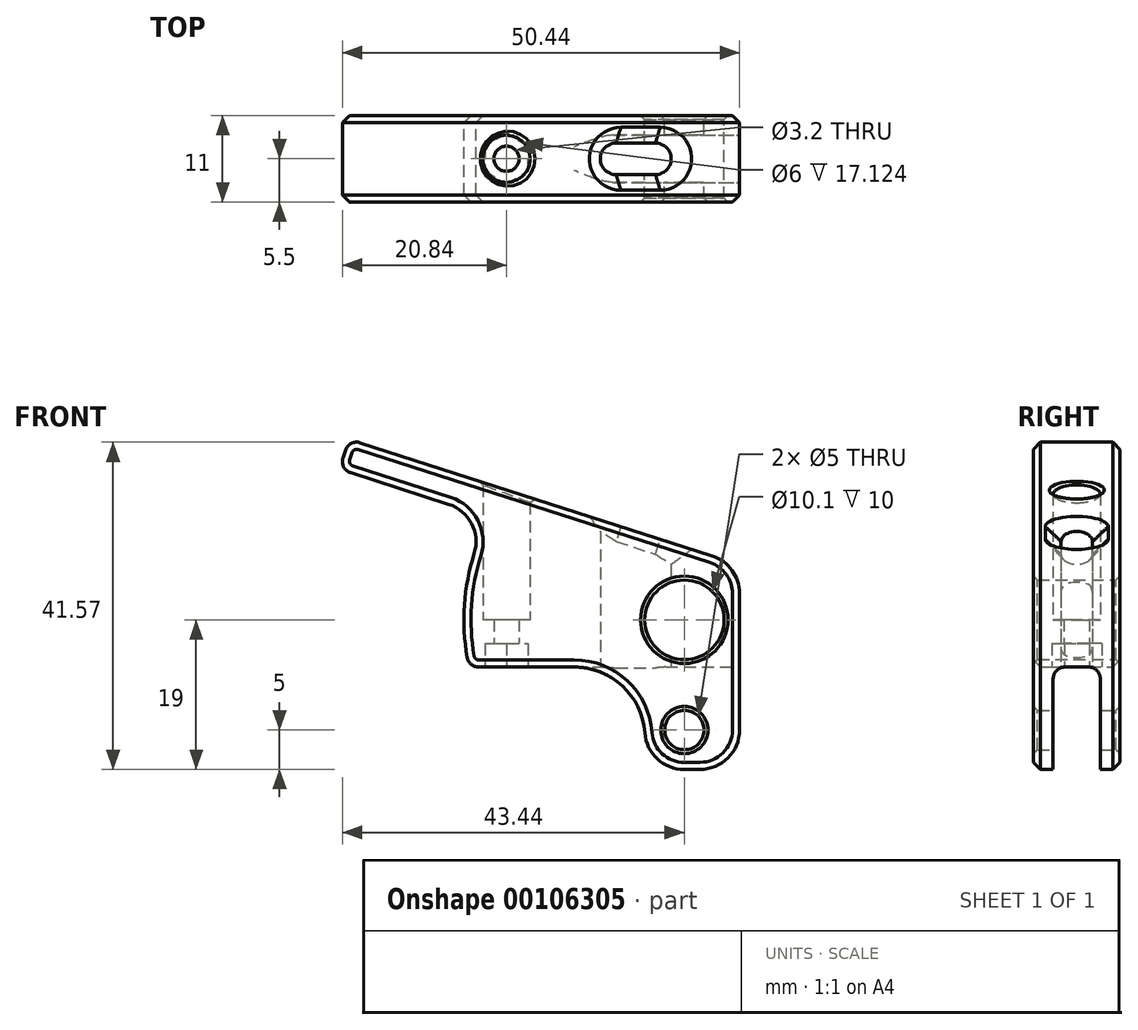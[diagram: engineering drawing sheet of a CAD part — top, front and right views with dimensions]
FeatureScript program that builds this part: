
annotation { "Feature Type Name" : "Feature", "Feature Type Description" : "" }
export const myFeature = defineFeature(function(context is Context, id is Id, definition is map)
    precondition{}
    {
        {
            var Q0;
            Q0=qCreatedBy(makeId("Front.planeOp"),FACE);
            var sketch = newSketch(context, id + "F0", { "sketchPlane" : qUnion([Q0])});
            skCircle(sketch, "E0", {"center": v(0, 0) * mm, "radius": 5.05 * mm});
            skCircle(sketch, "E1", {"center": v(0, -14) * mm, "radius": 2.5 * mm});
            skLineSegment(sketch, "E2.left", {"start": v(7, 7) * mm, "end": v(7, -19) * mm});
            skLineSegment(sketch, "E3.bottom", {"start": v(7, -19) * mm, "end": v(-5, -19) * mm});
            skLineSegment(sketch, "E3.right", {"start": v(-5, -19) * mm, "end": v(-5, -6) * mm});
            skLineSegment(sketch, "E4.trimOffspring", {"start": v(-5, -6) * mm, "end": v(-27.35, -6) * mm});
            skArc(sketch, "E5", {"start": v(-24.79, 13.02) * mm, "mid": v(-27.75, 3.74) * mm, "end": v(-27.35, -6) * mm});
            skLineSegment(sketch, "E6", {"start": v(-24.79, 13.02) * mm, "end": v(-43.83, 19.15) * mm});
            skLineSegment(sketch, "E7", {"start": v(-43.83, 19.15) * mm, "end": v(-42.6, 22.96) * mm});
            skLineSegment(sketch, "E8", {"start": v(-42.6, 22.96) * mm, "end": v(7, 7) * mm});
            skSolve(sketch);
        }
        {
            var Q0;
            Q0=qSketchRegion(id+"F0",true);
            extrude(context, id + "F1", {"entities" : qUnion([Q0]), "endBound" : BoundingType.SYMMETRIC, "depth" : 11 * mm});
        }
        {
            var Q0;
            Q0=makeQuery(id+"F1.opExtrude","SWEPT_FACE",FACE,{"disambiguationData":[OSD([sQuery(id+"F0.wireOp",EDGE,"E3.bottom")])]});
            var sketch = newSketch(context, id + "F2", { "sketchPlane" : qUnion([Q0])});
            skLineSegment(sketch, "E9.bottom", {"start": v(7, 3) * mm, "end": v(-7, 3) * mm});
            skLineSegment(sketch, "E9.top", {"start": v(7, -3) * mm, "end": v(-7, -3) * mm});
            skLineSegment(sketch, "E9.left", {"start": v(7, 3) * mm, "end": v(7, -3) * mm});
            skLineSegment(sketch, "E9.right", {"start": v(-7, 3) * mm, "end": v(-7, -3) * mm});
            skPoint(sketch, "E9.middle", {"position": v(0, 0) * mm});
            skSolve(sketch);
        }
        {
            var Q0;
            Q0=qSketchRegion(id+"F2",true);
            var Q1;
            Q1=makeQuery(id+"F1.opExtrude","SWEPT_FACE",FACE,{"disambiguationData":[OSD([sQuery(id+"F0.wireOp",EDGE,"E4.trimOffspring")])]});
            extrude(context, id + "F3", {"entities" : qUnion([Q0]), "operationType" : NewBodyOperationType.REMOVE, "endBound" : BoundingType.UP_TO_SURFACE, "oppositeDirection" : true, "endBoundEntityFace" : qUnion([Q1]), "depth" : 25 * mm});
        }
        {
            var Q0;
            Q0=makeQuery(id+"F3.boolean.opBoolean","MERGE",FACE,{"derivedFrom":[makeQuery(id+"F1.opExtrude","SWEPT_FACE",FACE,{"disambiguationData":[OSD([sQuery(id+"F0.wireOp",EDGE,"E4.trimOffspring")])]}),makeQuery(id+"F3.opExtrude","CAP_FACE",FACE,{"disambiguationData":[OSD([sQuery(id+"F2.wireOp",EDGE,"E9.bottom"),sQuery(id+"F2.wireOp",EDGE,"E9.top"),sQuery(id+"F2.wireOp",EDGE,"E9.left"),sQuery(id+"F2.wireOp",EDGE,"E9.right")])],"isStart":false})]});
            var sketch = newSketch(context, id + "F4", { "sketchPlane" : qUnion([Q0])});
            skLineSegment(sketch, "E10.bottom", {"start": v(-3.68, -2) * mm, "end": v(-8.68, -2) * mm});
            skLineSegment(sketch, "E10.top", {"start": v(-3.68, 2) * mm, "end": v(-8.68, 2) * mm});
            skPoint(sketch, "E10.middle", {"position": v(-6.18, 0) * mm});
            skArc(sketch, "E11", {"start": v(-8.68, 2) * mm, "mid": v(-10.68, 0) * mm, "end": v(-8.68, -2) * mm});
            skArc(sketch, "E12", {"start": v(-3.68, -2) * mm, "mid": v(-1.68, 0) * mm, "end": v(-3.68, 2) * mm});
            skSolve(sketch);
        }
        {
            var Q0;
            Q0=qSketchRegion(id+"F4",true);
            extrude(context, id + "F5", {"entities" : qUnion([Q0]), "operationType" : NewBodyOperationType.REMOVE, "endBound" : BoundingType.THROUGH_ALL, "oppositeDirection" : true, "depth" : 25 * mm});
        }
        {
            var Q0;
            {var subQ0=sQuery(id+"F0.wireOp",EDGE,"E4.trimOffspring");var subQ2=sQuery(id+"F2.wireOp",EDGE,"E9.bottom");var subQ3=sQuery(id+"F0.wireOp",EDGE,"E3.right");Q0=makeQuery(id+"F3.boolean.opBoolean","SPLIT",EDGE,{"disambiguationData":[TD([makeQuery(id+"F3.opExtrude","SWEPT_FACE",FACE,{"disambiguationData":[OSD([subQ2])]})])],"derivedFrom":makeQuery(id+"F1.opExtrude","SWEPT_EDGE",EDGE,{"disambiguationData":[OSD([subQ3,subQ0])]})});}
            var Q1;
            {var subQ0=sQuery(id+"F0.wireOp",EDGE,"E4.trimOffspring");var subQ1=sQuery(id+"F0.wireOp",EDGE,"E3.right");var subQ3=sQuery(id+"F2.wireOp",EDGE,"E9.top");Q1=makeQuery(id+"F3.boolean.opBoolean","SPLIT",EDGE,{"disambiguationData":[TD([makeQuery(id+"F3.opExtrude","SWEPT_FACE",FACE,{"disambiguationData":[OSD([subQ3])]})])],"derivedFrom":makeQuery(id+"F1.opExtrude","SWEPT_EDGE",EDGE,{"disambiguationData":[OSD([subQ1,subQ0])]})});}
            fillet(context, id + "F6", {"entities" : qUnion([Q0, Q1]), "radius" : 9 * mm, "tangentPropagation" : true, "allowEdgeOverflow" : false});
        }
        {
            var Q0;
            {var subQ0=sQuery(id+"F0.wireOp",EDGE,"E3.right");var subQ1=sQuery(id+"F0.wireOp",EDGE,"E3.bottom");Q0=makeQuery(id+"F3.boolean.opBoolean","SPLIT",EDGE,{"disambiguationData":[TD([makeQuery(id+"F3.opExtrude","SWEPT_FACE",FACE,{"disambiguationData":[OSD([sQuery(id+"F2.wireOp",EDGE,"E9.bottom")])]})])],"derivedFrom":makeQuery(id+"F1.opExtrude","SWEPT_EDGE",EDGE,{"disambiguationData":[OSD([subQ1,subQ0])]})});}
            var Q1;
            {var subQ0=sQuery(id+"F0.wireOp",EDGE,"E3.right");var subQ1=sQuery(id+"F0.wireOp",EDGE,"E3.bottom");Q1=makeQuery(id+"F3.boolean.opBoolean","SPLIT",EDGE,{"disambiguationData":[TD([makeQuery(id+"F3.opExtrude","SWEPT_FACE",FACE,{"disambiguationData":[OSD([sQuery(id+"F2.wireOp",EDGE,"E9.top")])]})])],"derivedFrom":makeQuery(id+"F1.opExtrude","SWEPT_EDGE",EDGE,{"disambiguationData":[OSD([subQ1,subQ0])]})});}
            fillet(context, id + "F7", {"entities" : qUnion([Q0, Q1]), "radius" : 5 * mm, "tangentPropagation" : true, "allowEdgeOverflow" : false});
        }
        {
            var Q0;
            {var subQ0=sQuery(id+"F0.wireOp",EDGE,"E3.bottom");var subQ1=sQuery(id+"F0.wireOp",EDGE,"E2.left");Q0=makeQuery(id+"F3.boolean.opBoolean","SPLIT",EDGE,{"disambiguationData":[TD([makeQuery(id+"F3.opExtrude","SWEPT_FACE",FACE,{"disambiguationData":[OSD([sQuery(id+"F2.wireOp",EDGE,"E9.bottom")])]})])],"derivedFrom":makeQuery(id+"F1.opExtrude","SWEPT_EDGE",EDGE,{"disambiguationData":[OSD([subQ1,subQ0])]})});}
            var Q1;
            {var subQ0=sQuery(id+"F0.wireOp",EDGE,"E3.bottom");var subQ1=sQuery(id+"F0.wireOp",EDGE,"E2.left");Q1=makeQuery(id+"F3.boolean.opBoolean","SPLIT",EDGE,{"disambiguationData":[TD([makeQuery(id+"F3.opExtrude","SWEPT_FACE",FACE,{"disambiguationData":[OSD([sQuery(id+"F2.wireOp",EDGE,"E9.top")])]})])],"derivedFrom":makeQuery(id+"F1.opExtrude","SWEPT_EDGE",EDGE,{"disambiguationData":[OSD([subQ1,subQ0])]})});}
            fillet(context, id + "F8", {"entities" : qUnion([Q0, Q1]), "radius" : 5 * mm, "tangentPropagation" : true, "allowEdgeOverflow" : false});
        }
        {
            var Q0;
            Q0=makeQuery(id+"F3.boolean.opBoolean","COPY",EDGE,{"derivedFrom":makeQuery(id+"F3.opExtrude","CAP_EDGE",EDGE,{"disambiguationData":[OSD([sQuery(id+"F2.wireOp",EDGE,"E9.bottom")])],"isStart":false})});
            var Q1;
            Q1=makeQuery(id+"F3.boolean.opBoolean","COPY",EDGE,{"derivedFrom":makeQuery(id+"F3.opExtrude","CAP_EDGE",EDGE,{"disambiguationData":[OSD([sQuery(id+"F2.wireOp",EDGE,"E9.top")])],"isStart":false})});
            fillet(context, id + "F9", {"entities" : qUnion([Q0, Q1]), "radius" : 1.5 * mm, "tangentPropagation" : true, "allowEdgeOverflow" : false});
        }
        {
            var Q0;
            Q0=makeQuery(id+"F1.opExtrude","SWEPT_EDGE",EDGE,{"disambiguationData":[OSD([sQuery(id+"F0.wireOp",EDGE,"E5"),sQuery(id+"F0.wireOp",EDGE,"E6")])]});
            fillet(context, id + "F10", {"entities" : qUnion([Q0]), "radius" : 5 * mm, "tangentPropagation" : true, "allowEdgeOverflow" : false});
        }
        {
            var Q0;
            Q0=makeQuery(id+"F1.opExtrude","SWEPT_EDGE",EDGE,{"disambiguationData":[OSD([sQuery(id+"F0.wireOp",EDGE,"E2.bottom"),sQuery(id+"F0.wireOp",EDGE,"E2.left")])]});
            fillet(context, id + "F11", {"entities" : qUnion([Q0]), "radius" : 5 * mm, "tangentPropagation" : true, "allowEdgeOverflow" : false});
        }
        {
            var Q0;
            Q0=makeQuery(id+"F9.opFillet","SPLIT",FACE,{"disambiguationData":[OD(0.0)],"derivedFrom":makeQuery(id+"F3.boolean.opBoolean","MERGE",FACE,{"derivedFrom":[makeQuery(id+"F1.opExtrude","SWEPT_FACE",FACE,{"disambiguationData":[OSD([sQuery(id+"F0.wireOp",EDGE,"E4.trimOffspring")])]}),makeQuery(id+"F3.opExtrude","CAP_FACE",FACE,{"disambiguationData":[OSD([sQuery(id+"F2.wireOp",EDGE,"E9.bottom"),sQuery(id+"F2.wireOp",EDGE,"E9.top"),sQuery(id+"F2.wireOp",EDGE,"E9.left"),sQuery(id+"F2.wireOp",EDGE,"E9.right")])],"isStart":false})]})});
            var sketch = newSketch(context, id + "F12", { "sketchPlane" : qUnion([Q0])});
            skCircle(sketch, "E13.cCircle", {"center": v(-22.6, 0) * mm, "radius": 2.75 * mm, "construction": true});
            skLineSegment(sketch, "E13.0", {"start": v(-19.85, 1.59) * mm, "end": v(-19.85, -1.59) * mm});
            skLineSegment(sketch, "E13.1", {"start": v(-19.85, -1.59) * mm, "end": v(-22.6, -3.18) * mm});
            skLineSegment(sketch, "E13.2", {"start": v(-22.6, -3.18) * mm, "end": v(-25.35, -1.59) * mm});
            skLineSegment(sketch, "E13.3", {"start": v(-25.35, -1.59) * mm, "end": v(-25.35, 1.59) * mm});
            skLineSegment(sketch, "E13.4", {"start": v(-25.35, 1.59) * mm, "end": v(-22.6, 3.18) * mm});
            skLineSegment(sketch, "E13.5", {"start": v(-22.6, 3.18) * mm, "end": v(-19.85, 1.59) * mm});
            skPoint(sketch, "E13.0.midPoint", {"position": v(-19.85, 0) * mm});
            skSolve(sketch);
        }
        {
            var Q0;
            Q0=qSketchRegion(id+"F12",true);
            extrude(context, id + "F13", {"entities" : qUnion([Q0]), "operationType" : NewBodyOperationType.REMOVE, "oppositeDirection" : true, "depth" : 3 * mm});
        }
        {
            var Q0;
            Q0=makeQuery(id+"F13.boolean.opBoolean","COPY",FACE,{"derivedFrom":makeQuery(id+"F13.opExtrude","CAP_FACE",FACE,{"disambiguationData":[OSD([sQuery(id+"F12.wireOp",EDGE,"E13.0"),sQuery(id+"F12.wireOp",EDGE,"E13.1"),sQuery(id+"F12.wireOp",EDGE,"E13.2"),sQuery(id+"F12.wireOp",EDGE,"E13.3"),sQuery(id+"F12.wireOp",EDGE,"E13.4"),sQuery(id+"F12.wireOp",EDGE,"E13.5")])],"isStart":false})});
            var sketch = newSketch(context, id + "F14", { "sketchPlane" : qUnion([Q0])});
            skCircle(sketch, "E14", {"center": v(-22.6, 0) * mm, "radius": 1.6 * mm});
            skLineSegment(sketch, "E15", {"start": v(-25.35, 0) * mm, "end": v(-19.85, 0) * mm, "construction": true});
            skSolve(sketch);
        }
        {
            var Q0;
            Q0=qSketchRegion(id+"F14",true);
            extrude(context, id + "F15", {"entities" : qUnion([Q0]), "operationType" : NewBodyOperationType.REMOVE, "endBound" : BoundingType.THROUGH_ALL, "oppositeDirection" : true, "depth" : 25 * mm});
        }
        {
            var Q0;
            Q0=qCreatedBy(makeId("Top.planeOp"),FACE);
            var sketch = newSketch(context, id + "F16", { "sketchPlane" : qUnion([Q0])});
            skCircle(sketch, "E16", {"center": v(-22.6, 0) * mm, "radius": 3 * mm});
            skSolve(sketch);
        }
        {
            var Q0;
            Q0=qSketchRegion(id+"F16",true);
            extrude(context, id + "F17", {"entities" : qUnion([Q0]), "operationType" : NewBodyOperationType.REMOVE, "endBound" : BoundingType.THROUGH_ALL, "depth" : 25 * mm});
        }
        {
            var Q0;
            Q0=makeQuery(id+"F1.opExtrude","SWEPT_EDGE",EDGE,{"disambiguationData":[OSD([sQuery(id+"F0.wireOp",EDGE,"E4.trimOffspring"),sQuery(id+"F0.wireOp",EDGE,"E5")])]});
            var Q1;
            Q1=makeQuery(id+"F1.opExtrude","SWEPT_EDGE",EDGE,{"disambiguationData":[OSD([sQuery(id+"F0.wireOp",EDGE,"E6"),sQuery(id+"F0.wireOp",EDGE,"E7")])]});
            var Q2;
            Q2=makeQuery(id+"F1.opExtrude","SWEPT_EDGE",EDGE,{"disambiguationData":[OSD([sQuery(id+"F0.wireOp",EDGE,"E7"),sQuery(id+"F0.wireOp",EDGE,"E8")])]});
            fillet(context, id + "F18", {"entities" : qUnion([Q0, Q1, Q2]), "radius" : 1.5 * mm, "tangentPropagation" : true, "allowEdgeOverflow" : false});
        }
        {
            var Q0;
            Q0=makeQuery(id+"F1.opExtrude","CAP_EDGE",EDGE,{"disambiguationData":[OSD([sQuery(id+"F0.wireOp",EDGE,"E8")])],"isStart":true});
            var Q1;
            Q1=makeQuery(id+"F1.opExtrude","CAP_EDGE",EDGE,{"disambiguationData":[OSD([sQuery(id+"F0.wireOp",EDGE,"E4.trimOffspring")])],"isStart":false});
            chamfer(context, id + "F19", {"entities" : qUnion([Q0, Q1]), "width" : .9 * mm, "tangentPropagation" : true});
        }
        {
            var Q0;
            Q0=makeQuery(id+"F17.boolean.opBoolean","INTERSECT",EDGE,{"derivedFrom":[makeQuery(id+"F1.opExtrude","SWEPT_FACE",FACE,{"disambiguationData":[OSD([sQuery(id+"F0.wireOp",EDGE,"E8")])]}),makeQuery(id+"F17.opExtrude","SWEPT_FACE",FACE,{"disambiguationData":[OSD([sQuery(id+"F16.wireOp",EDGE,"E16")])]})]});
            var Q1;
            Q1=makeQuery(id+"F1.opExtrude","CAP_EDGE",EDGE,{"disambiguationData":[OSD([sQuery(id+"F0.wireOp",EDGE,"E0")])],"isStart":false});
            var Q2;
            Q2=makeQuery(id+"F1.opExtrude","CAP_EDGE",EDGE,{"disambiguationData":[OSD([sQuery(id+"F0.wireOp",EDGE,"E1")])],"isStart":false});
            var Q3;
            Q3=makeQuery(id+"F1.opExtrude","CAP_EDGE",EDGE,{"disambiguationData":[OSD([sQuery(id+"F0.wireOp",EDGE,"E0")])],"isStart":true});
            var Q4;
            Q4=makeQuery(id+"F1.opExtrude","CAP_EDGE",EDGE,{"disambiguationData":[OSD([sQuery(id+"F0.wireOp",EDGE,"E1")])],"isStart":true});
            var Q5;
            Q5=makeQuery(id+"F5.boolean.opBoolean","COPY",EDGE,{"derivedFrom":makeQuery(id+"F5.opExtrude","CAP_EDGE",EDGE,{"disambiguationData":[OSD([sQuery(id+"F4.wireOp",EDGE,"E11")])],"isStart":true})});
            var Q6;
            Q6=makeQuery(id+"F15.boolean.opBoolean","COPY",EDGE,{"derivedFrom":makeQuery(id+"F15.opExtrude","CAP_EDGE",EDGE,{"disambiguationData":[OSD([sQuery(id+"F14.wireOp",EDGE,"E14")])],"isStart":true})});
            var Q7;
            Q7=makeQuery(id+"F13.boolean.opBoolean","COPY",EDGE,{"derivedFrom":makeQuery(id+"F13.opExtrude","CAP_EDGE",EDGE,{"disambiguationData":[OSD([sQuery(id+"F12.wireOp",EDGE,"E13.5")])],"isStart":true})});
            var Q8;
            Q8=makeQuery(id+"F13.boolean.opBoolean","COPY",EDGE,{"derivedFrom":makeQuery(id+"F13.opExtrude","CAP_EDGE",EDGE,{"disambiguationData":[OSD([sQuery(id+"F12.wireOp",EDGE,"E13.0")])],"isStart":true})});
            var Q9;
            Q9=makeQuery(id+"F13.boolean.opBoolean","COPY",EDGE,{"derivedFrom":makeQuery(id+"F13.opExtrude","CAP_EDGE",EDGE,{"disambiguationData":[OSD([sQuery(id+"F12.wireOp",EDGE,"E13.1")])],"isStart":true})});
            var Q10;
            Q10=makeQuery(id+"F13.boolean.opBoolean","COPY",EDGE,{"derivedFrom":makeQuery(id+"F13.opExtrude","CAP_EDGE",EDGE,{"disambiguationData":[OSD([sQuery(id+"F12.wireOp",EDGE,"E13.2")])],"isStart":true})});
            var Q11;
            Q11=makeQuery(id+"F13.boolean.opBoolean","COPY",EDGE,{"derivedFrom":makeQuery(id+"F13.opExtrude","CAP_EDGE",EDGE,{"disambiguationData":[OSD([sQuery(id+"F12.wireOp",EDGE,"E13.3")])],"isStart":true})});
            var Q12;
            Q12=makeQuery(id+"F13.boolean.opBoolean","COPY",EDGE,{"derivedFrom":makeQuery(id+"F13.opExtrude","CAP_EDGE",EDGE,{"disambiguationData":[OSD([sQuery(id+"F12.wireOp",EDGE,"E13.4")])],"isStart":true})});
            chamfer(context, id + "F20", {"entities" : qUnion([Q0, Q1, Q2, Q3, Q4, Q5, Q6, Q7, Q8, Q9, Q10, Q11, Q12]), "width" : .5 * mm, "tangentPropagation" : true});
        }
        {
            var Q0;
            Q0=makeQuery(id+"F5.boolean.opBoolean","INTERSECT",EDGE,{"derivedFrom":[makeQuery(id+"F1.opExtrude","SWEPT_FACE",FACE,{"disambiguationData":[OSD([sQuery(id+"F0.wireOp",EDGE,"E8")])]}),makeQuery(id+"F5.opExtrude","SWEPT_FACE",FACE,{"disambiguationData":[OSD([sQuery(id+"F4.wireOp",EDGE,"E10.bottom")])]})]});
            chamfer(context, id + "F21", {"entities" : qUnion([Q0]), "width" : 2 * mm, "tangentPropagation" : true});
        }
    });
